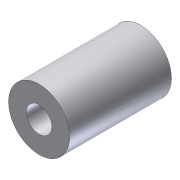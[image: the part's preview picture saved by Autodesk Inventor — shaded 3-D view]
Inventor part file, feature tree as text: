
AUTODESK INVENTOR PART (.ipt)
format: ipt  version: 2012 (Build 160160000, 160)  size: 81,408 bytes
history: native  units: in
note: dims shown in document units (in); Inventor stores cm internally (conversion verified against a paired STEP export)
features: extrude x1, sketch x1
ambient origin geometry x8: Origin, YZ Plane, XZ Plane, XY Plane, X Axis, Y Axis, Z Axis, Center Point
bodies: Solid1 (feature_tree)
feature tree (2):
  extrude  "Extrusion1"  Depth=1.5in
  sketch  "Sketch1"  dims[d0=0.625in d1=1.5in d2=2.5in d3=0.0in]
